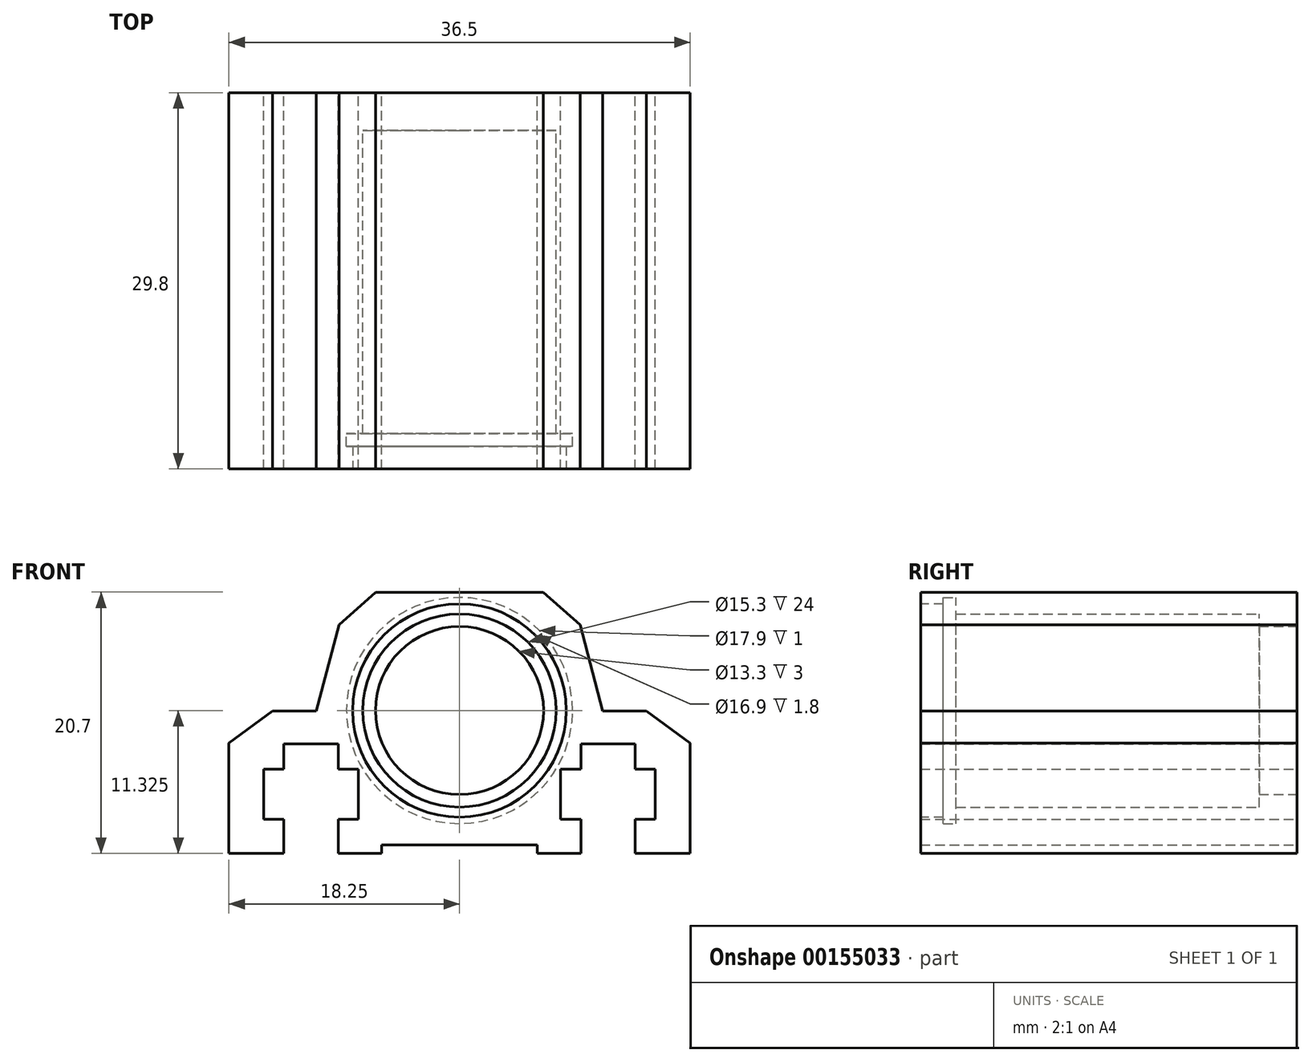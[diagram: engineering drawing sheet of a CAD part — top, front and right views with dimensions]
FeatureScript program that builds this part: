
annotation { "Feature Type Name" : "Feature", "Feature Type Description" : "" }
export const myFeature = defineFeature(function(context is Context, id is Id, definition is map)
    precondition{}
    {
        {
            var Q0;
            Q0=qCreatedBy(makeId("Front.planeOp"),FACE);
            var sketch = newSketch(context, id + "F0", { "sketchPlane" : qUnion([Q0])});
            skLineSegment(sketch, "E0", {"start": v(0, 0) * mm, "end": v(0, 26.85) * mm, "construction": true});
            skLineSegment(sketch, "E1", {"start": v(6.16, 0) * mm, "end": v(9.6, 0) * mm});
            skLineSegment(sketch, "E2", {"start": v(9.6, 0) * mm, "end": v(9.6, 2.7) * mm});
            skLineSegment(sketch, "E3", {"start": v(9.6, 2.7) * mm, "end": v(8, 2.7) * mm});
            skLineSegment(sketch, "E4", {"start": v(8, 2.7) * mm, "end": v(8, 6.7) * mm});
            skLineSegment(sketch, "E5", {"start": v(8, 6.7) * mm, "end": v(9.6, 6.7) * mm});
            skLineSegment(sketch, "E6", {"start": v(15.5, 6.7) * mm, "end": v(15.5, 2.7) * mm});
            skLineSegment(sketch, "E7", {"start": v(15.5, 2.7) * mm, "end": v(13.9, 2.7) * mm});
            skLineSegment(sketch, "E8", {"start": v(13.9, 2.7) * mm, "end": v(13.9, 0) * mm});
            skLineSegment(sketch, "E9", {"start": v(13.9, 0) * mm, "end": v(18.25, 0) * mm});
            skLineSegment(sketch, "E10", {"start": v(18.25, 0) * mm, "end": v(18.25, 8.74) * mm});
            skLineSegment(sketch, "E11", {"start": v(14.8, 11.3) * mm, "end": v(11.33, 11.3) * mm});
            skLineSegment(sketch, "E12", {"start": v(13.9, 6.7) * mm, "end": v(13.9, 8.67) * mm});
            skLineSegment(sketch, "E13", {"start": v(13.9, 8.67) * mm, "end": v(9.6, 8.67) * mm});
            skLineSegment(sketch, "E14", {"start": v(9.6, 8.67) * mm, "end": v(9.6, 6.7) * mm});
            skLineSegment(sketch, "E15.trimOffspring", {"start": v(13.9, 6.7) * mm, "end": v(15.5, 6.7) * mm});
            skLineSegment(sketch, "E16", {"start": v(6.16, 0) * mm, "end": v(6.16, 0.68) * mm});
            skLineSegment(sketch, "E17", {"start": v(6.16, 0.68) * mm, "end": v(0, 0.68) * mm});
            skCircle(sketch, "E18", {"center": v(0, 11.33) * mm, "radius": 7.65 * mm});
            skLineSegment(sketch, "E19", {"start": v(11.33, 11.3) * mm, "end": v(9.54, 18.1) * mm});
            skLineSegment(sketch, "E20", {"start": v(6.64, 20.7) * mm, "end": v(0, 20.7) * mm});
            skLineSegment(sketch, "E21.MirrorCS", {"start": v(-13.9, 6.7) * mm, "end": v(-15.5, 6.7) * mm});
            skLineSegment(sketch, "E22.MirrorCS", {"start": v(-9.6, 8.67) * mm, "end": v(-9.6, 6.7) * mm});
            skLineSegment(sketch, "E23.MirrorCS", {"start": v(-6.16, 0) * mm, "end": v(-6.16, 0.68) * mm});
            skLineSegment(sketch, "E24.MirrorCS", {"start": v(-13.9, 6.7) * mm, "end": v(-13.9, 8.67) * mm});
            skLineSegment(sketch, "E25.MirrorCS", {"start": v(-9.6, 2.7) * mm, "end": v(-8, 2.7) * mm});
            skLineSegment(sketch, "E26.MirrorCS", {"start": v(-15.5, 2.7) * mm, "end": v(-13.9, 2.7) * mm});
            skLineSegment(sketch, "E27.MirrorCS", {"start": v(-8, 6.7) * mm, "end": v(-9.6, 6.7) * mm});
            skLineSegment(sketch, "E28.MirrorCS", {"start": v(-6.16, 0) * mm, "end": v(-9.6, 0) * mm});
            skLineSegment(sketch, "E29.MirrorCS", {"start": v(-13.9, 8.67) * mm, "end": v(-9.6, 8.67) * mm});
            skLineSegment(sketch, "E30.MirrorCS", {"start": v(-9.6, 0) * mm, "end": v(-9.6, 2.7) * mm});
            skLineSegment(sketch, "E31.MirrorCS", {"start": v(-11.33, 11.3) * mm, "end": v(-9.54, 18.1) * mm});
            skLineSegment(sketch, "E32.MirrorCS", {"start": v(-18.25, 0) * mm, "end": v(-18.25, 8.74) * mm});
            skLineSegment(sketch, "E33.MirrorCS", {"start": v(-13.9, 0) * mm, "end": v(-18.25, 0) * mm});
            skLineSegment(sketch, "E34.MirrorCS", {"start": v(-6.64, 20.7) * mm, "end": v(0, 20.7) * mm});
            skLineSegment(sketch, "E35.MirrorCS", {"start": v(-14.8, 11.3) * mm, "end": v(-11.33, 11.3) * mm});
            skLineSegment(sketch, "E36.MirrorCS", {"start": v(-6.16, 0.68) * mm, "end": v(0, 0.68) * mm});
            skLineSegment(sketch, "E37.MirrorCS", {"start": v(-13.9, 2.7) * mm, "end": v(-13.9, 0) * mm});
            skLineSegment(sketch, "E38.MirrorCS", {"start": v(-8, 2.7) * mm, "end": v(-8, 6.7) * mm});
            skLineSegment(sketch, "E39.MirrorCS", {"start": v(-15.5, 6.7) * mm, "end": v(-15.5, 2.7) * mm});
            skLineSegment(sketch, "E40", {"start": v(18.25, 8.74) * mm, "end": v(14.8, 11.3) * mm});
            skLineSegment(sketch, "E41", {"start": v(9.54, 18.1) * mm, "end": v(6.64, 20.7) * mm});
            skPoint(sketch, "E42.orphan", {"position": v(8.85, 20.7) * mm});
            skPoint(sketch, "E43.orphan", {"position": v(18.25, 11.3) * mm});
            skLineSegment(sketch, "E44.MirrorCS", {"start": v(-9.54, 18.1) * mm, "end": v(-6.64, 20.7) * mm});
            skLineSegment(sketch, "E45.MirrorCS", {"start": v(-18.25, 8.74) * mm, "end": v(-14.8, 11.3) * mm});
            skPoint(sketch, "E46.orphan", {"position": v(-8.85, 20.7) * mm});
            skPoint(sketch, "E47.orphan", {"position": v(-18.25, 11.3) * mm});
            skSolve(sketch);
        }
        {
            var Q0;
            Q0=makeQuery(id+"F0.imprint","IMPRINT",FACE,{"disambiguationData":[TD([[makeQuery(id+"F0.imprint","IMPRINT",EDGE,{"derivedFrom":sQuery(id+"F0.wireOp",EDGE,"E1")}),1.0]])]});
            extrude(context, id + "F1", {"entities" : qUnion([Q0]), "depth" : (23.8 + 6) * mm, "symmetric" : true});
        }
        {
            var Q0;
            Q0=makeQuery(id+"F1.opExtrude","CAP_FACE",FACE,{"disambiguationData":[OSD([sQuery(id+"F0.wireOp",EDGE,"E1"),sQuery(id+"F0.wireOp",EDGE,"E2"),sQuery(id+"F0.wireOp",EDGE,"E3"),sQuery(id+"F0.wireOp",EDGE,"E4"),sQuery(id+"F0.wireOp",EDGE,"E5"),sQuery(id+"F0.wireOp",EDGE,"E6"),sQuery(id+"F0.wireOp",EDGE,"E7"),sQuery(id+"F0.wireOp",EDGE,"E8"),sQuery(id+"F0.wireOp",EDGE,"E9"),sQuery(id+"F0.wireOp",EDGE,"E10"),sQuery(id+"F0.wireOp",EDGE,"E11"),sQuery(id+"F0.wireOp",EDGE,"E12"),sQuery(id+"F0.wireOp",EDGE,"E13"),sQuery(id+"F0.wireOp",EDGE,"E14"),sQuery(id+"F0.wireOp",EDGE,"E15.trimOffspring"),sQuery(id+"F0.wireOp",EDGE,"E16"),sQuery(id+"F0.wireOp",EDGE,"E17"),sQuery(id+"F0.wireOp",EDGE,"E18"),sQuery(id+"F0.wireOp",EDGE,"E19"),sQuery(id+"F0.wireOp",EDGE,"E20"),sQuery(id+"F0.wireOp",EDGE,"E21.MirrorCS"),sQuery(id+"F0.wireOp",EDGE,"E22.MirrorCS"),sQuery(id+"F0.wireOp",EDGE,"E23.MirrorCS"),sQuery(id+"F0.wireOp",EDGE,"E24.MirrorCS"),sQuery(id+"F0.wireOp",EDGE,"E25.MirrorCS"),sQuery(id+"F0.wireOp",EDGE,"E26.MirrorCS"),sQuery(id+"F0.wireOp",EDGE,"E27.MirrorCS"),sQuery(id+"F0.wireOp",EDGE,"E28.MirrorCS"),sQuery(id+"F0.wireOp",EDGE,"E29.MirrorCS"),sQuery(id+"F0.wireOp",EDGE,"E30.MirrorCS"),sQuery(id+"F0.wireOp",EDGE,"E31.MirrorCS"),sQuery(id+"F0.wireOp",EDGE,"E32.MirrorCS"),sQuery(id+"F0.wireOp",EDGE,"E33.MirrorCS"),sQuery(id+"F0.wireOp",EDGE,"E34.MirrorCS"),sQuery(id+"F0.wireOp",EDGE,"E35.MirrorCS"),sQuery(id+"F0.wireOp",EDGE,"E36.MirrorCS"),sQuery(id+"F0.wireOp",EDGE,"E37.MirrorCS"),sQuery(id+"F0.wireOp",EDGE,"E38.MirrorCS"),sQuery(id+"F0.wireOp",EDGE,"E39.MirrorCS")])],"isStart":false});
            cPlane(context, id + "F2", {"entities" : qUnion([Q0]), "cplaneType" : CPlaneType.OFFSET, "offset" : (3 - 0.2) * mm, "oppositeDirection" : true, "width" : 150 * mm, "height" : 150 * mm});
        }
        {
            var Q0;
            Q0=qCreatedBy(id+"F2.planeOp",FACE);
            var sketch = newSketch(context, id + "F3", { "sketchPlane" : qUnion([Q0])});
            skCircle(sketch, "E48", {"center": v(0, 11.33) * mm, "radius": 8.95 * mm});
            skSolve(sketch);
        }
        {
            var Q0;
            Q0=makeQuery(id+"F3.imprint","IMPRINT",FACE,{"disambiguationData":[TD([[makeQuery(id+"F3.imprint","IMPRINT",EDGE,{"derivedFrom":sQuery(id+"F3.wireOp",EDGE,"E48")}),1.0]])]});
            var Q1;
            Q1=sQuery(id+"F3.wireOp",EDGE,"E48");
            extrude(context, id + "F4", {"entities" : qUnion([Q0]), "operationType" : NewBodyOperationType.REMOVE, "surfaceEntities" : qUnion([Q1]), "depth" : 1 * mm});
        }
        {
            var Q0;
            Q0=makeQuery(id+"F1.opExtrude","CAP_FACE",FACE,{"disambiguationData":[OSD([sQuery(id+"F0.wireOp",EDGE,"E1"),sQuery(id+"F0.wireOp",EDGE,"E2"),sQuery(id+"F0.wireOp",EDGE,"E3"),sQuery(id+"F0.wireOp",EDGE,"E4"),sQuery(id+"F0.wireOp",EDGE,"E5"),sQuery(id+"F0.wireOp",EDGE,"E6"),sQuery(id+"F0.wireOp",EDGE,"E7"),sQuery(id+"F0.wireOp",EDGE,"E8"),sQuery(id+"F0.wireOp",EDGE,"E9"),sQuery(id+"F0.wireOp",EDGE,"E10"),sQuery(id+"F0.wireOp",EDGE,"E11"),sQuery(id+"F0.wireOp",EDGE,"E12"),sQuery(id+"F0.wireOp",EDGE,"E13"),sQuery(id+"F0.wireOp",EDGE,"E14"),sQuery(id+"F0.wireOp",EDGE,"E15.trimOffspring"),sQuery(id+"F0.wireOp",EDGE,"E16"),sQuery(id+"F0.wireOp",EDGE,"E17"),sQuery(id+"F0.wireOp",EDGE,"E18"),sQuery(id+"F0.wireOp",EDGE,"E19"),sQuery(id+"F0.wireOp",EDGE,"E20"),sQuery(id+"F0.wireOp",EDGE,"E21.MirrorCS"),sQuery(id+"F0.wireOp",EDGE,"E22.MirrorCS"),sQuery(id+"F0.wireOp",EDGE,"E23.MirrorCS"),sQuery(id+"F0.wireOp",EDGE,"E24.MirrorCS"),sQuery(id+"F0.wireOp",EDGE,"E25.MirrorCS"),sQuery(id+"F0.wireOp",EDGE,"E26.MirrorCS"),sQuery(id+"F0.wireOp",EDGE,"E27.MirrorCS"),sQuery(id+"F0.wireOp",EDGE,"E28.MirrorCS"),sQuery(id+"F0.wireOp",EDGE,"E29.MirrorCS"),sQuery(id+"F0.wireOp",EDGE,"E30.MirrorCS"),sQuery(id+"F0.wireOp",EDGE,"E31.MirrorCS"),sQuery(id+"F0.wireOp",EDGE,"E32.MirrorCS"),sQuery(id+"F0.wireOp",EDGE,"E33.MirrorCS"),sQuery(id+"F0.wireOp",EDGE,"E34.MirrorCS"),sQuery(id+"F0.wireOp",EDGE,"E35.MirrorCS"),sQuery(id+"F0.wireOp",EDGE,"E36.MirrorCS"),sQuery(id+"F0.wireOp",EDGE,"E37.MirrorCS"),sQuery(id+"F0.wireOp",EDGE,"E38.MirrorCS"),sQuery(id+"F0.wireOp",EDGE,"E39.MirrorCS")])],"isStart":true});
            var sketch = newSketch(context, id + "F5", { "sketchPlane" : qUnion([Q0])});
            skCircle(sketch, "E49", {"center": v(0, 11.33) * mm, "radius": 6.65 * mm});
            skSolve(sketch);
        }
        {
            var Q0;
            Q0=makeQuery(id+"F5.imprint","IMPRINT",FACE,{"disambiguationData":[TD([[makeQuery(id+"F5.imprint","IMPRINT",EDGE,{"derivedFrom":sQuery(id+"F5.wireOp",EDGE,"E49")}),-1.0]])]});
            extrude(context, id + "F6", {"entities" : qUnion([Q0]), "operationType" : NewBodyOperationType.ADD, "oppositeDirection" : true, "depth" : 3 * mm});
        }
        {
            var Q0;
            Q0=makeQuery(id+"F1.opExtrude","CAP_FACE",FACE,{"disambiguationData":[OSD([sQuery(id+"F0.wireOp",EDGE,"E1"),sQuery(id+"F0.wireOp",EDGE,"E2"),sQuery(id+"F0.wireOp",EDGE,"E3"),sQuery(id+"F0.wireOp",EDGE,"E4"),sQuery(id+"F0.wireOp",EDGE,"E5"),sQuery(id+"F0.wireOp",EDGE,"E6"),sQuery(id+"F0.wireOp",EDGE,"E7"),sQuery(id+"F0.wireOp",EDGE,"E8"),sQuery(id+"F0.wireOp",EDGE,"E9"),sQuery(id+"F0.wireOp",EDGE,"E10"),sQuery(id+"F0.wireOp",EDGE,"E11"),sQuery(id+"F0.wireOp",EDGE,"E12"),sQuery(id+"F0.wireOp",EDGE,"E13"),sQuery(id+"F0.wireOp",EDGE,"E14"),sQuery(id+"F0.wireOp",EDGE,"E15.trimOffspring"),sQuery(id+"F0.wireOp",EDGE,"E16"),sQuery(id+"F0.wireOp",EDGE,"E17"),sQuery(id+"F0.wireOp",EDGE,"E18"),sQuery(id+"F0.wireOp",EDGE,"E19"),sQuery(id+"F0.wireOp",EDGE,"E20"),sQuery(id+"F0.wireOp",EDGE,"E21.MirrorCS"),sQuery(id+"F0.wireOp",EDGE,"E22.MirrorCS"),sQuery(id+"F0.wireOp",EDGE,"E23.MirrorCS"),sQuery(id+"F0.wireOp",EDGE,"E24.MirrorCS"),sQuery(id+"F0.wireOp",EDGE,"E25.MirrorCS"),sQuery(id+"F0.wireOp",EDGE,"E26.MirrorCS"),sQuery(id+"F0.wireOp",EDGE,"E27.MirrorCS"),sQuery(id+"F0.wireOp",EDGE,"E28.MirrorCS"),sQuery(id+"F0.wireOp",EDGE,"E29.MirrorCS"),sQuery(id+"F0.wireOp",EDGE,"E30.MirrorCS"),sQuery(id+"F0.wireOp",EDGE,"E31.MirrorCS"),sQuery(id+"F0.wireOp",EDGE,"E32.MirrorCS"),sQuery(id+"F0.wireOp",EDGE,"E33.MirrorCS"),sQuery(id+"F0.wireOp",EDGE,"E34.MirrorCS"),sQuery(id+"F0.wireOp",EDGE,"E35.MirrorCS"),sQuery(id+"F0.wireOp",EDGE,"E36.MirrorCS"),sQuery(id+"F0.wireOp",EDGE,"E37.MirrorCS"),sQuery(id+"F0.wireOp",EDGE,"E38.MirrorCS"),sQuery(id+"F0.wireOp",EDGE,"E39.MirrorCS"),sQuery(id+"F0.wireOp",EDGE,"E40"),sQuery(id+"F0.wireOp",EDGE,"E41"),sQuery(id+"F0.wireOp",EDGE,"E44.MirrorCS"),sQuery(id+"F0.wireOp",EDGE,"E45.MirrorCS")])],"isStart":false});
            var sketch = newSketch(context, id + "F7", { "sketchPlane" : qUnion([Q0])});
            skCircle(sketch, "E50", {"center": v(0, 11.33) * mm, "radius": 8.45 * mm});
            skSolve(sketch);
        }
        {
            var Q0;
            Q0 = qSketchRegion(id + "F7", true);
            var Q1;
            Q1=makeQuery(id+"F4.boolean.opBoolean","COPY",FACE,{"derivedFrom":makeQuery(id+"F4.opExtrude","CAP_FACE",FACE,{"disambiguationData":[OSD([sQuery(id+"F3.wireOp",EDGE,"E48")])],"isStart":true})});
            extrude(context, id + "F8", {"entities" : qUnion([Q0]), "operationType" : NewBodyOperationType.REMOVE, "endBound" : BoundingType.UP_TO_SURFACE, "oppositeDirection" : true, "endBoundEntityFace" : qUnion([Q1]), "depth" : 3 * mm});
        }
    });
